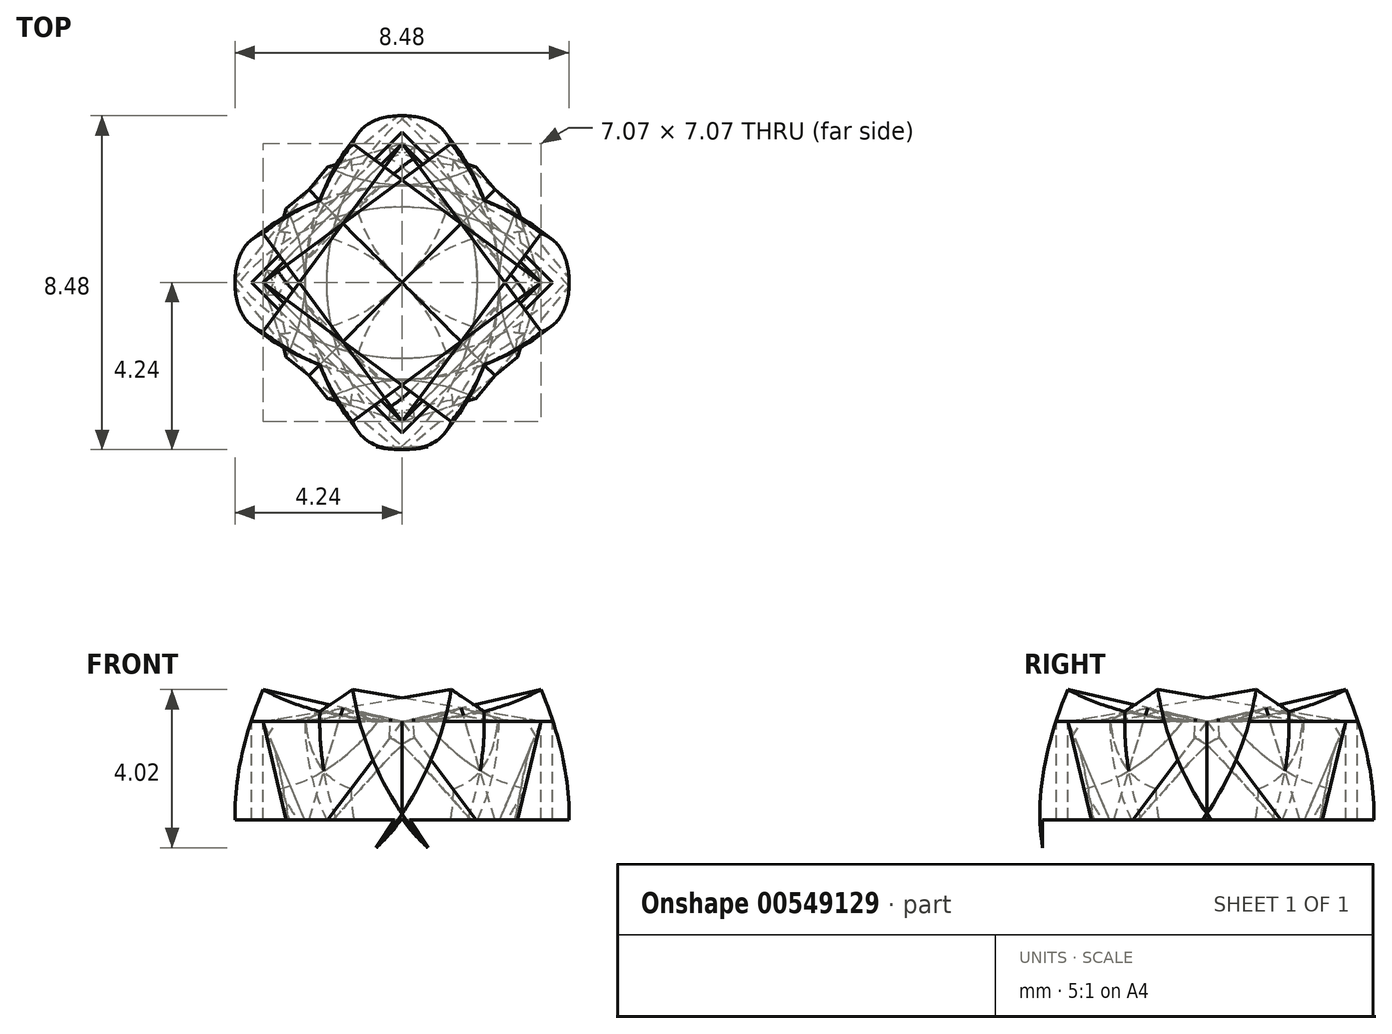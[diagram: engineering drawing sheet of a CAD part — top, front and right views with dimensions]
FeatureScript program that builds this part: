
annotation { "Feature Type Name" : "Feature", "Feature Type Description" : "" }
export const myFeature = defineFeature(function(context is Context, id is Id, definition is map)
    precondition{}
    {
        {
            var Q0;
            Q0=qCreatedBy(makeId("Front.planeOp"),FACE);
            var sketch = newSketch(context, id + "F0", { "sketchPlane" : qUnion([Q0])});
            skLineSegment(sketch, "E0", {"start": v(0, 0) * mm, "end": v(6, 0) * mm});
            skLineSegment(sketch, "E1", {"start": v(0, 0) * mm, "end": v(2.34, -5.52) * mm});
            skArc(sketch, "E2", {"start": v(2.34, -5.52) * mm, "mid": v(5, -3.31) * mm, "end": v(6, 0) * mm});
            skLineSegment(sketch, "E3", {"start": v(0, 0) * mm, "end": v(0, 3.06) * mm, "construction": true});
            skLineSegment(sketch, "E4", {"start": v(0, 0) * mm, "end": v(2.25, 3.36) * mm, "construction": true});
            skLineSegment(sketch, "E5", {"start": v(0, 0) * mm, "end": v(0, -2.5) * mm, "construction": true});
            skLineSegment(sketch, "E6", {"start": v(0, -2.5) * mm, "end": v(1.06, -2.5) * mm, "construction": true});
            skLineSegment(sketch, "E7.trimOffspring", {"start": v(5.4, -2.5) * mm, "end": v(5.45, -2.5) * mm, "construction": true});
            skSolve(sketch);
        }
        {
            var Q0;
            Q0 = qSketchRegion(id + "F0", true);
            var Q1;
            Q1=sQuery(id+"F0.wireOp",EDGE,"E4");
            revolve(context, id + "F1", {"entities" : qUnion([Q0]), "axis" : qUnion([Q1]), "revolveType" : RevolveType.SYMMETRIC, "angle" : 90 * degree});
        }
        {
            var Q0;
            Q0=qCreatedBy(makeId("Top.planeOp"),FACE);
            var sketch = newSketch(context, id + "F2", { "sketchPlane" : qUnion([Q0])});
            skLineSegment(sketch, "E8", {"start": v(0, 0) * mm, "end": v(3.54, 3.54) * mm});
            skLineSegment(sketch, "E9", {"start": v(3.54, 3.54) * mm, "end": v(7.07, 0) * mm});
            skLineSegment(sketch, "E10", {"start": v(7.07, 0) * mm, "end": v(3.54, -3.54) * mm});
            skLineSegment(sketch, "E11", {"start": v(3.54, -3.54) * mm, "end": v(0, 0) * mm});
            skLineSegment(sketch, "E12.0", {"start": v(3.54, 3.82) * mm, "end": v(7.35, 0) * mm});
            skLineSegment(sketch, "E12.1", {"start": v(-0.28, 0) * mm, "end": v(3.54, 3.82) * mm});
            skLineSegment(sketch, "E12.2", {"start": v(3.54, -3.82) * mm, "end": v(-0.28, 0) * mm});
            skLineSegment(sketch, "E12.3", {"start": v(7.35, 0) * mm, "end": v(3.54, -3.82) * mm});
            skSolve(sketch);
        }
        {
            var Q0;
            Q0 = qSketchRegion(id + "F2", true);
            extrude(context, id + "F3", {"entities" : qUnion([Q0]), "oppositeDirection" : true, "depth" : 2.5 * mm, "offsetDistance" : 25 * mm});
        }
        {
            var Q0;
            Q0=makeQuery(id+"F1.opRevolve","SWEPT_BODY",BODY,{"disambiguationData":[OSD([sQuery(id+"F0.wireOp",EDGE,"E0"),sQuery(id+"F0.wireOp",EDGE,"E1"),sQuery(id+"F0.wireOp",EDGE,"E2")])]});
            var Q1;
            Q1=makeQuery(id+"F3.opExtrude","SWEPT_BODY",BODY,{"disambiguationData":[OSD([sQuery(id+"F2.wireOp",EDGE,"E8"),sQuery(id+"F2.wireOp",EDGE,"E9"),sQuery(id+"F2.wireOp",EDGE,"E10"),sQuery(id+"F2.wireOp",EDGE,"E11"),sQuery(id+"F2.wireOp",EDGE,"E12.0"),sQuery(id+"F2.wireOp",EDGE,"E12.1"),sQuery(id+"F2.wireOp",EDGE,"E12.2"),sQuery(id+"F2.wireOp",EDGE,"E12.3")])]});
            transform(context, id + "F4", {"entities" : qUnion([Q0, Q1]), "transformType" : TransformType.TRANSLATION_3D, "dx" : (-sqrt(2) * 5 / 2) * mm, "dy" : 0 * mm, "dz" : 0 * mm, "makeCopy" : false});
        }
        {
            var Q0;
            Q0=makeQuery(id+"F1.opRevolve","SWEPT_BODY",BODY,{"disambiguationData":[OSD([sQuery(id+"F0.wireOp",EDGE,"E0"),sQuery(id+"F0.wireOp",EDGE,"E1"),sQuery(id+"F0.wireOp",EDGE,"E2")])]});
            var Q1;
            Q1=sQuery(id+"F0.wireOp",EDGE,"E3");
            transform(context, id + "F5", {"entities" : qUnion([Q0]), "transformType" : TransformType.ROTATION, "transformAxis" : qUnion([Q1]), "angle" : 90 * degree, "makeCopy" : true});
        }
        {
            var Q0;
            Q0=makeQuery(id+"F1.opRevolve","SWEPT_BODY",BODY,{"disambiguationData":[OSD([sQuery(id+"F0.wireOp",EDGE,"E0"),sQuery(id+"F0.wireOp",EDGE,"E1"),sQuery(id+"F0.wireOp",EDGE,"E2")])]});
            var Q1;
            Q1=makeQuery(id+"F5.opPattern","COPY",BODY,{"derivedFrom":makeQuery(id+"F1.opRevolve","SWEPT_BODY",BODY,{"disambiguationData":[OSD([sQuery(id+"F0.wireOp",EDGE,"E0"),sQuery(id+"F0.wireOp",EDGE,"E1"),sQuery(id+"F0.wireOp",EDGE,"E2")])]}),"instanceName":"1"});
            var Q2;
            Q2=sQuery(id+"F0.wireOp",EDGE,"E3");
            transform(context, id + "F6", {"entities" : qUnion([Q0, Q1]), "transformType" : TransformType.ROTATION, "transformAxis" : qUnion([Q2]), "angle" : 180 * degree, "makeCopy" : true});
        }
        {
            var Q0;
            Q0=makeQuery(id+"F1.opRevolve","SWEPT_BODY",BODY,{"disambiguationData":[OSD([sQuery(id+"F0.wireOp",EDGE,"E0"),sQuery(id+"F0.wireOp",EDGE,"E1"),sQuery(id+"F0.wireOp",EDGE,"E2")])]});
            var Q1;
            Q1=makeQuery(id+"F5.opPattern","COPY",BODY,{"derivedFrom":makeQuery(id+"F1.opRevolve","SWEPT_BODY",BODY,{"disambiguationData":[OSD([sQuery(id+"F0.wireOp",EDGE,"E0"),sQuery(id+"F0.wireOp",EDGE,"E1"),sQuery(id+"F0.wireOp",EDGE,"E2")])]}),"instanceName":"1"});
            booleanBodies(context, id + "F7", {"operationType" : BooleanOperationType.INTERSECTION, "tools" : qUnion([Q0, Q1]), "keepTools" : true});
        }
        {
            var Q0;
            Q0=makeQuery(id+"F5.opPattern","COPY",BODY,{"derivedFrom":makeQuery(id+"F1.opRevolve","SWEPT_BODY",BODY,{"disambiguationData":[OSD([sQuery(id+"F0.wireOp",EDGE,"E0"),sQuery(id+"F0.wireOp",EDGE,"E1"),sQuery(id+"F0.wireOp",EDGE,"E2")])]}),"instanceName":"1"});
            var Q1;
            Q1=makeQuery(id+"F6.opPattern","COPY",BODY,{"derivedFrom":makeQuery(id+"F1.opRevolve","SWEPT_BODY",BODY,{"disambiguationData":[OSD([sQuery(id+"F0.wireOp",EDGE,"E0"),sQuery(id+"F0.wireOp",EDGE,"E1"),sQuery(id+"F0.wireOp",EDGE,"E2")])]}),"instanceName":"1"});
            booleanBodies(context, id + "F8", {"operationType" : BooleanOperationType.INTERSECTION, "tools" : qUnion([Q0, Q1]), "keepTools" : true});
        }
        {
            var Q0;
            Q0=makeQuery(id+"F6.opPattern","COPY",BODY,{"derivedFrom":makeQuery(id+"F1.opRevolve","SWEPT_BODY",BODY,{"disambiguationData":[OSD([sQuery(id+"F0.wireOp",EDGE,"E0"),sQuery(id+"F0.wireOp",EDGE,"E1"),sQuery(id+"F0.wireOp",EDGE,"E2")])]}),"instanceName":"1"});
            var Q1;
            Q1=makeQuery(id+"F6.opPattern","COPY",BODY,{"derivedFrom":makeQuery(id+"F5.opPattern","COPY",BODY,{"derivedFrom":makeQuery(id+"F1.opRevolve","SWEPT_BODY",BODY,{"disambiguationData":[OSD([sQuery(id+"F0.wireOp",EDGE,"E0"),sQuery(id+"F0.wireOp",EDGE,"E1"),sQuery(id+"F0.wireOp",EDGE,"E2")])]}),"instanceName":"1"}),"instanceName":"1"});
            booleanBodies(context, id + "F9", {"operationType" : BooleanOperationType.INTERSECTION, "tools" : qUnion([Q0, Q1]), "keepTools" : true});
        }
        {
            var Q0;
            Q0=makeQuery(id+"F6.opPattern","COPY",BODY,{"derivedFrom":makeQuery(id+"F5.opPattern","COPY",BODY,{"derivedFrom":makeQuery(id+"F1.opRevolve","SWEPT_BODY",BODY,{"disambiguationData":[OSD([sQuery(id+"F0.wireOp",EDGE,"E0"),sQuery(id+"F0.wireOp",EDGE,"E1"),sQuery(id+"F0.wireOp",EDGE,"E2")])]}),"instanceName":"1"}),"instanceName":"1"});
            var Q1;
            Q1=makeQuery(id+"F1.opRevolve","SWEPT_BODY",BODY,{"disambiguationData":[OSD([sQuery(id+"F0.wireOp",EDGE,"E0"),sQuery(id+"F0.wireOp",EDGE,"E1"),sQuery(id+"F0.wireOp",EDGE,"E2")])]});
            booleanBodies(context, id + "F10", {"operationType" : BooleanOperationType.INTERSECTION, "tools" : qUnion([Q0, Q1]), "keepTools" : true});
        }
        {
            var Q0;
            {var subQ0=makeQuery(id+"F1.opRevolve","SWEPT_BODY",BODY,{"disambiguationData":[OSD([sQuery(id+"F0.wireOp",EDGE,"E0"),sQuery(id+"F0.wireOp",EDGE,"E1"),sQuery(id+"F0.wireOp",EDGE,"E2")])]});Q0=makeQuery(id+"F7.opBoolean","INTERSECT",BODY,{"derivedFrom":[subQ0,makeQuery(id+"F5.opPattern","COPY",BODY,{"derivedFrom":subQ0,"instanceName":"1"})]});}
            var Q1;
            {var subQ0=makeQuery(id+"F1.opRevolve","SWEPT_BODY",BODY,{"disambiguationData":[OSD([sQuery(id+"F0.wireOp",EDGE,"E0"),sQuery(id+"F0.wireOp",EDGE,"E1"),sQuery(id+"F0.wireOp",EDGE,"E2")])]});Q1=makeQuery(id+"F8.opBoolean","INTERSECT",BODY,{"derivedFrom":[makeQuery(id+"F5.opPattern","COPY",BODY,{"derivedFrom":subQ0,"instanceName":"1"}),makeQuery(id+"F6.opPattern","COPY",BODY,{"derivedFrom":subQ0,"instanceName":"1"})]});}
            var Q2;
            {var subQ0=makeQuery(id+"F1.opRevolve","SWEPT_BODY",BODY,{"disambiguationData":[OSD([sQuery(id+"F0.wireOp",EDGE,"E0"),sQuery(id+"F0.wireOp",EDGE,"E1"),sQuery(id+"F0.wireOp",EDGE,"E2")])]});Q2=makeQuery(id+"F9.opBoolean","INTERSECT",BODY,{"derivedFrom":[makeQuery(id+"F6.opPattern","COPY",BODY,{"derivedFrom":subQ0,"instanceName":"1"}),makeQuery(id+"F6.opPattern","COPY",BODY,{"derivedFrom":makeQuery(id+"F5.opPattern","COPY",BODY,{"derivedFrom":subQ0,"instanceName":"1"}),"instanceName":"1"})]});}
            var Q3;
            {var subQ0=makeQuery(id+"F1.opRevolve","SWEPT_BODY",BODY,{"disambiguationData":[OSD([sQuery(id+"F0.wireOp",EDGE,"E0"),sQuery(id+"F0.wireOp",EDGE,"E1"),sQuery(id+"F0.wireOp",EDGE,"E2")])]});Q3=makeQuery(id+"F10.opBoolean","INTERSECT",BODY,{"derivedFrom":[subQ0,makeQuery(id+"F6.opPattern","COPY",BODY,{"derivedFrom":makeQuery(id+"F5.opPattern","COPY",BODY,{"derivedFrom":subQ0,"instanceName":"1"}),"instanceName":"1"})]});}
            booleanBodies(context, id + "F11", {"operationType" : BooleanOperationType.INTERSECTION, "tools" : qUnion([Q0, Q1, Q2, Q3]), "keepTools" : true});
        }
        {
            var Q0;
            Q0=makeQuery(id+"F3.opExtrude","CAP_FACE",FACE,{"disambiguationData":[OSD([sQuery(id+"F2.wireOp",EDGE,"E8"),sQuery(id+"F2.wireOp",EDGE,"E9"),sQuery(id+"F2.wireOp",EDGE,"E10"),sQuery(id+"F2.wireOp",EDGE,"E11"),sQuery(id+"F2.wireOp",EDGE,"E12.0"),sQuery(id+"F2.wireOp",EDGE,"E12.1"),sQuery(id+"F2.wireOp",EDGE,"E12.2"),sQuery(id+"F2.wireOp",EDGE,"E12.3")])],"isStart":false});
            var sketch = newSketch(context, id + "F12", { "sketchPlane" : qUnion([Q0])});
            skLineSegment(sketch, "E13.bottom", {"start": v(-5.77, 4.17) * mm, "end": v(7.64, 4.17) * mm});
            skLineSegment(sketch, "E13.top", {"start": v(-5.77, -6.38) * mm, "end": v(7.64, -6.38) * mm});
            skLineSegment(sketch, "E13.left", {"start": v(-5.77, 4.17) * mm, "end": v(-5.77, -6.38) * mm});
            skLineSegment(sketch, "E13.right", {"start": v(7.64, 4.17) * mm, "end": v(7.64, -6.38) * mm});
            skSolve(sketch);
        }
        {
            var Q0;
            Q0 = qSketchRegion(id + "F12", true);
            extrude(context, id + "F13", {"entities" : qUnion([Q0]), "operationType" : NewBodyOperationType.REMOVE, "depth" : 25 * mm, "offsetDistance" : 25 * mm});
        }
    });
